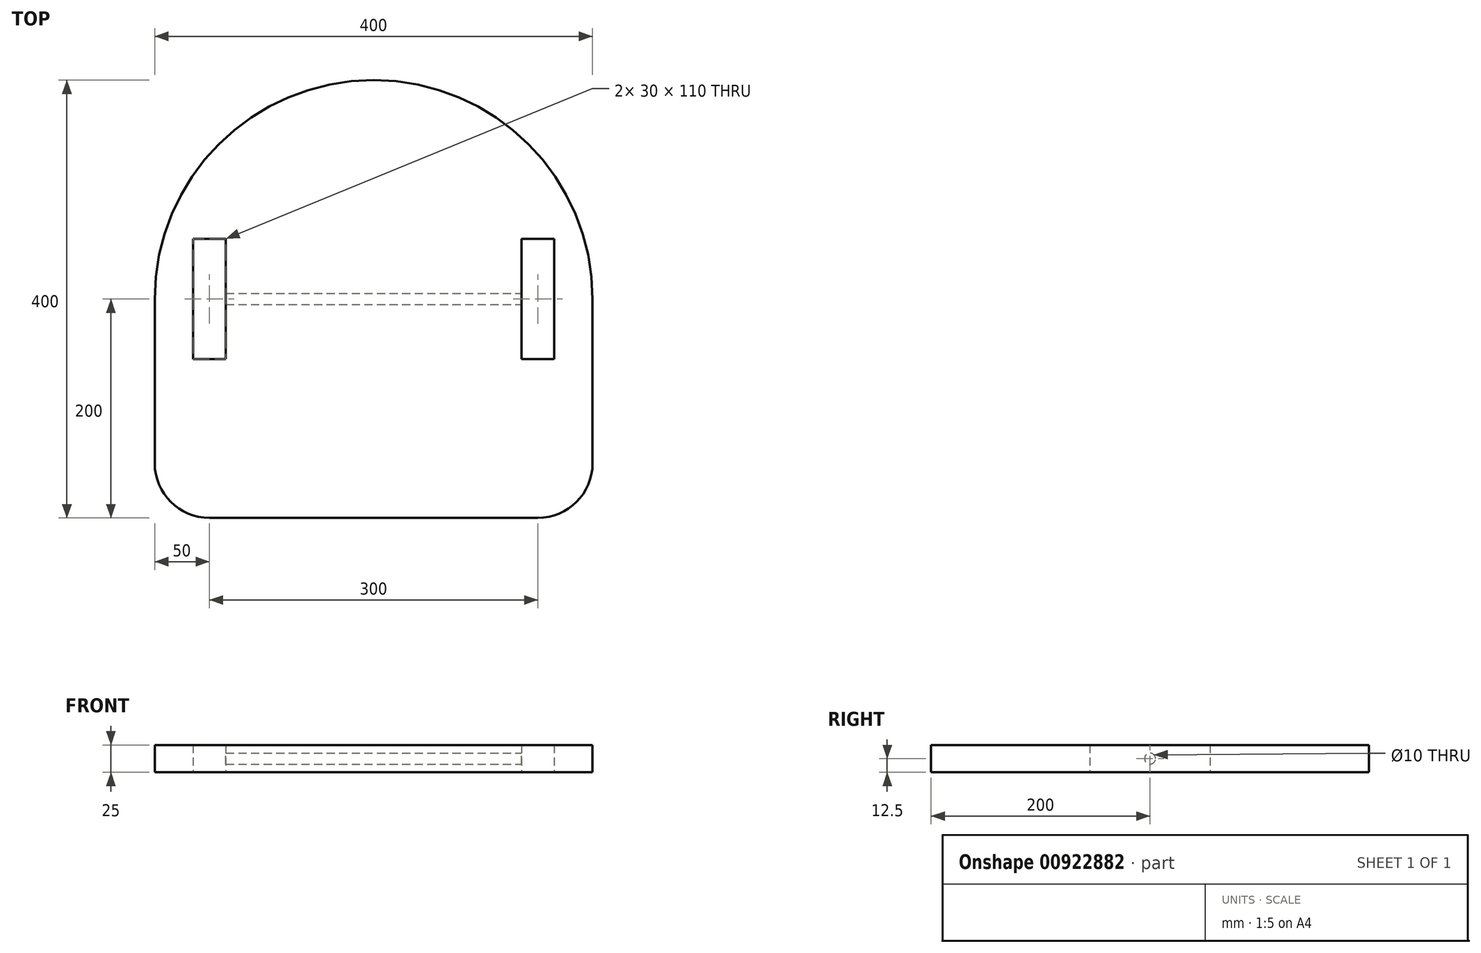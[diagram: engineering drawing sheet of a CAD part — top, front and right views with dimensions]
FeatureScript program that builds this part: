
annotation { "Feature Type Name" : "Feature", "Feature Type Description" : "" }
export const myFeature = defineFeature(function(context is Context, id is Id, definition is map)
    precondition{}
    {
        {
            var Q0;
            Q0=qCreatedBy(makeId("Top.planeOp"),FACE);
            var sketch = newSketch(context, id + "F0", { "sketchPlane" : qUnion([Q0])});
            skArc(sketch, "E0", {"start": v(200, 0) * mm, "mid": v(0, 200) * mm, "end": v(-200, 0) * mm});
            skLineSegment(sketch, "E1", {"start": v(200, 0) * mm, "end": v(200, -200) * mm});
            skLineSegment(sketch, "E2", {"start": v(200, -200) * mm, "end": v(-200, -200) * mm});
            skLineSegment(sketch, "E3", {"start": v(-200, 0) * mm, "end": v(-200, -200) * mm});
            skLineSegment(sketch, "E4.bottom", {"start": v(165, 55) * mm, "end": v(135, 55) * mm});
            skLineSegment(sketch, "E4.top", {"start": v(165, -55) * mm, "end": v(135, -55) * mm});
            skLineSegment(sketch, "E4.left", {"start": v(165, 55) * mm, "end": v(165, -55) * mm});
            skLineSegment(sketch, "E4.right", {"start": v(135, 55) * mm, "end": v(135, -55) * mm});
            skPoint(sketch, "E4.middle", {"position": v(150, 0) * mm});
            skLineSegment(sketch, "E5.bottom", {"start": v(-135, 55) * mm, "end": v(-165, 55) * mm});
            skLineSegment(sketch, "E5.top", {"start": v(-135, -55) * mm, "end": v(-165, -55) * mm});
            skLineSegment(sketch, "E5.left", {"start": v(-135, 55) * mm, "end": v(-135, -55) * mm});
            skLineSegment(sketch, "E5.right", {"start": v(-165, 55) * mm, "end": v(-165, -55) * mm});
            skPoint(sketch, "E5.middle", {"position": v(-150, 0) * mm});
            skSolve(sketch);
        }
        {
            var Q0;
            Q0=makeQuery(id+"F0.imprint","IMPRINT",FACE,{"disambiguationData":[TD([[makeQuery(id+"F0.imprint","IMPRINT",EDGE,{"derivedFrom":sQuery(id+"F0.wireOp",EDGE,"E0")}),1.0]])]});
            extrude(context, id + "F1", {"entities" : qUnion([Q0]), "depth" : 25 * mm, "offsetDistance" : 25 * mm});
        }
        {
            var Q0;
            Q0=makeQuery(id+"F1.opExtrude","SWEPT_EDGE",EDGE,{"disambiguationData":[OSD([sQuery(id+"F0.wireOp",EDGE,"E1"),sQuery(id+"F0.wireOp",EDGE,"E2")])]});
            var Q1;
            Q1=makeQuery(id+"F1.opExtrude","SWEPT_EDGE",EDGE,{"disambiguationData":[OSD([sQuery(id+"F0.wireOp",EDGE,"E2"),sQuery(id+"F0.wireOp",EDGE,"E3")])]});
            fillet(context, id + "F2", {"entities" : qUnion([Q0, Q1]), "radius" : 50 * mm, "tangentPropagation" : true, "allowEdgeOverflow" : false});
        }
        {
            var Q0;
            Q0=makeQuery(id+"F1.opExtrude","SWEPT_FACE",FACE,{"disambiguationData":[OSD([sQuery(id+"F0.wireOp",EDGE,"E4.right")])]});
            var sketch = newSketch(context, id + "F3", { "sketchPlane" : qUnion([Q0])});
            skCircle(sketch, "E6", {"center": v(0, 12.5) * mm, "radius": 5 * mm});
            skPoint(sketch, "E6.centerSnap0", {"position": v(0, 25) * mm});
            skPoint(sketch, "E6.centerSnap1", {"position": v(-55, 12.5) * mm});
            skSolve(sketch);
        }
        {
            var Q0;
            Q0 = qSketchRegion(id + "F3", true);
            extrude(context, id + "F4", {"entities" : qUnion([Q0]), "operationType" : NewBodyOperationType.REMOVE, "endBound" : BoundingType.UP_TO_NEXT, "oppositeDirection" : true, "depth" : 25 * mm, "offsetDistance" : 25 * mm});
        }
    });
